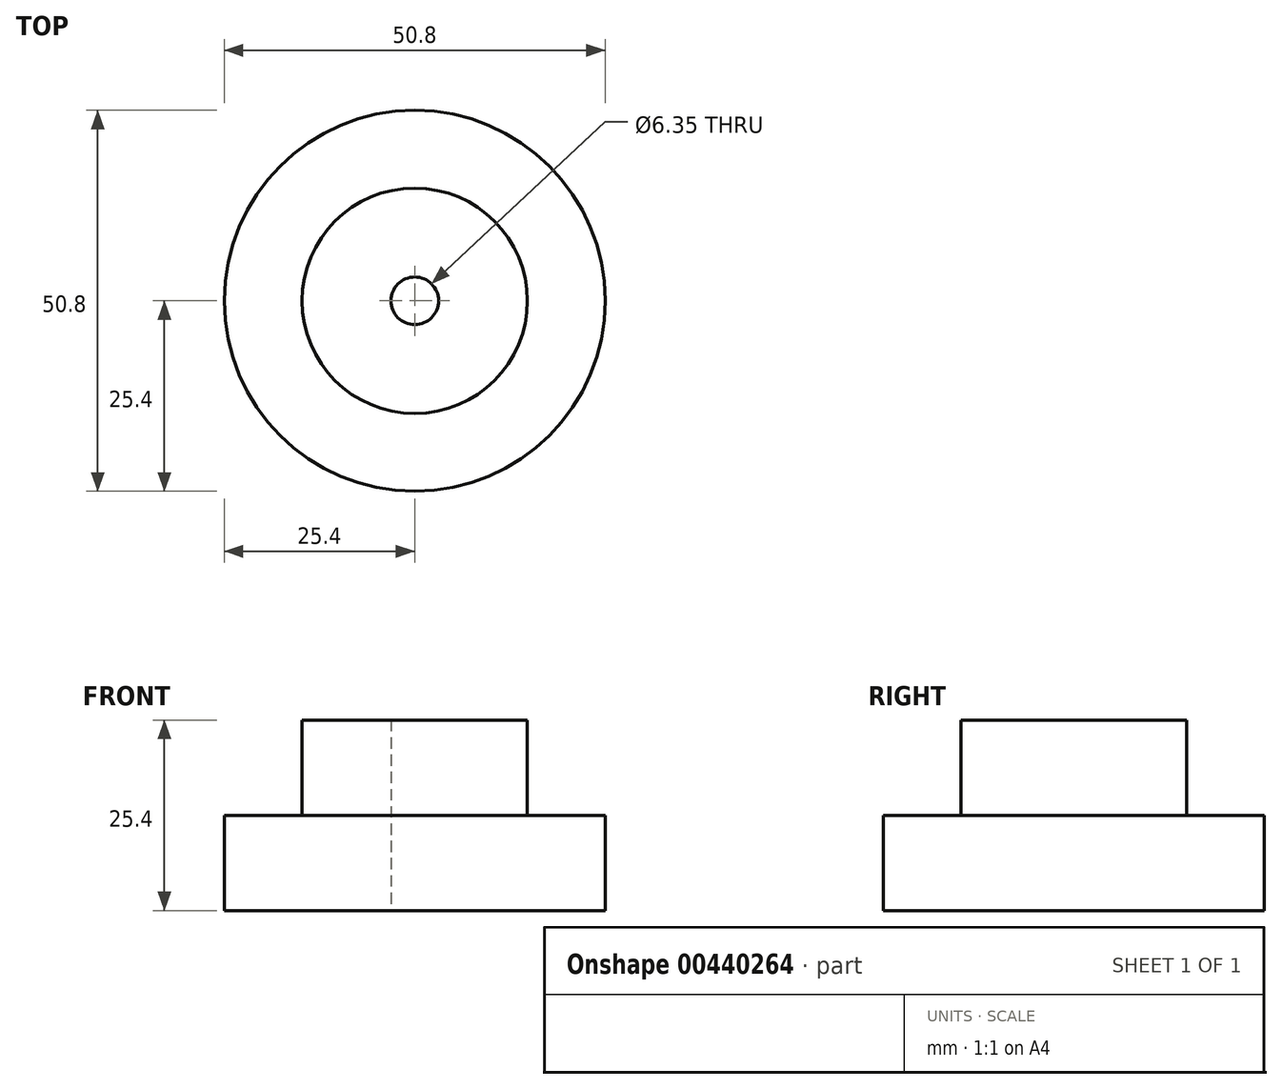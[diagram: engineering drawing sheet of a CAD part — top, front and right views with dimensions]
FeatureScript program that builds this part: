
annotation { "Feature Type Name" : "Feature", "Feature Type Description" : "" }
export const myFeature = defineFeature(function(context is Context, id is Id, definition is map)
    precondition{}
    {
        {
            var Q0;
            Q0=qCreatedBy(makeId("Front.planeOp"),FACE);
            var sketch = newSketch(context, id + "F0", { "sketchPlane" : qUnion([Q0])});
            skLineSegment(sketch, "E0", {"start": v(-3.17, 0) * mm, "end": v(-25.4, 0) * mm});
            skLineSegment(sketch, "E1", {"start": v(-25.4, 0) * mm, "end": v(-25.4, 12.7) * mm});
            skLineSegment(sketch, "E2", {"start": v(-25.4, 12.7) * mm, "end": v(-15.02, 12.7) * mm});
            skLineSegment(sketch, "E3", {"start": v(-15.02, 12.7) * mm, "end": v(-15.02, 25.4) * mm});
            skLineSegment(sketch, "E4", {"start": v(-15.02, 25.4) * mm, "end": v(-3.18, 25.4) * mm});
            skLineSegment(sketch, "E5.0", {"start": v(-3.18, 25.4) * mm, "end": v(-3.17, 0) * mm});
            skLineSegment(sketch, "E6", {"start": v(0, 0) * mm, "end": v(0, 41.56) * mm, "construction": true});
            skSolve(sketch);
        }
        {
            var Q0;
            Q0=makeQuery(id+"F0.imprint","IMPRINT",FACE,{"disambiguationData":[TD([[makeQuery(id+"F0.imprint","IMPRINT",EDGE,{"derivedFrom":sQuery(id+"F0.wireOp",EDGE,"E0")}),-1.0]])]});
            var Q1;
            Q1=sQuery(id+"F0.wireOp",EDGE,"E6");
            revolve(context, id + "F1", {"entities" : qUnion([Q0]), "axis" : qUnion([Q1]), "revolveType" : RevolveType.FULL});
        }
    });
